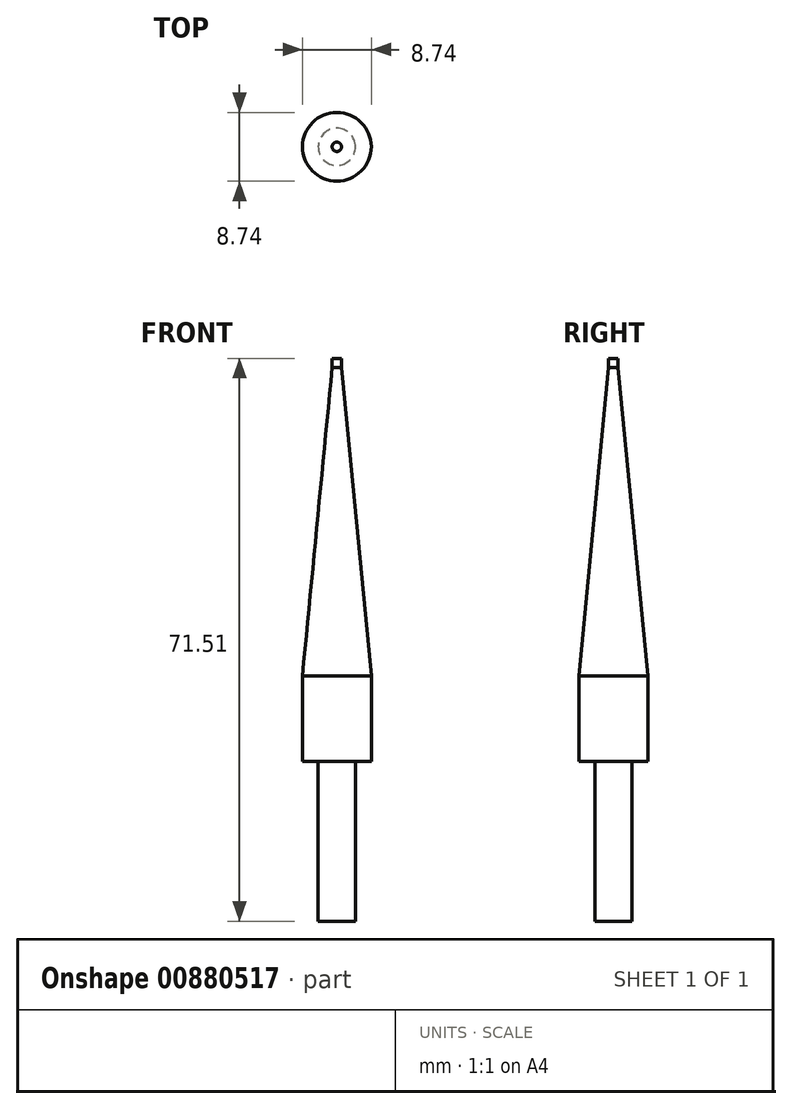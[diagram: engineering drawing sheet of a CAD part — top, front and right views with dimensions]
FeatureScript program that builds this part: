
annotation { "Feature Type Name" : "Feature", "Feature Type Description" : "" }
export const myFeature = defineFeature(function(context is Context, id is Id, definition is map)
    precondition{}
    {
        {
            var Q0;
            Q0=qCreatedBy(makeId("Front.planeOp"),FACE);
            var sketch = newSketch(context, id + "F0", { "sketchPlane" : qUnion([Q0])});
            skLineSegment(sketch, "E0", {"start": v(0.6, 55.68) * mm, "end": v(4.37, 16.5) * mm});
            skLineSegment(sketch, "E1", {"start": v(4.37, 16.5) * mm, "end": v(4.37, 5.65) * mm});
            skLineSegment(sketch, "E2", {"start": v(4.37, 5.65) * mm, "end": v(2.36, 5.65) * mm});
            skLineSegment(sketch, "E3", {"start": v(2.36, 5.65) * mm, "end": v(2.36, -14.67) * mm});
            skLineSegment(sketch, "E4", {"start": v(2.36, -14.67) * mm, "end": v(0, -14.67) * mm});
            skLineSegment(sketch, "E5", {"start": v(0, -14.67) * mm, "end": v(0, 56.84) * mm});
            skLineSegment(sketch, "E6", {"start": v(0, 56.84) * mm, "end": v(1, 56.84) * mm});
            skLineSegment(sketch, "E7", {"start": v(0, 56.84) * mm, "end": v(0, -14.67) * mm});
            skLineSegment(sketch, "E8", {"start": v(0.6, 55.67) * mm, "end": v(0.6, 55.68) * mm});
            skLineSegment(sketch, "E9", {"start": v(0.6, 55.68) * mm, "end": v(0.6, 60.51) * mm});
            skLineSegment(sketch, "E10", {"start": v(0.6, 60.51) * mm, "end": v(1, 56.84) * mm});
            skSolve(sketch);
        }
        {
            var Q0;
            Q0=makeQuery(id+"F0.imprint","IMPRINT",FACE,{"disambiguationData":[TD([[makeQuery(id+"F0.imprint","IMPRINT",EDGE,{"derivedFrom":sQuery(id+"F0.wireOp",EDGE,"E0")}),-1.0]])]});
            var Q1;
            Q1=sQuery(id+"F0.wireOp",EDGE,"E5");
            revolve(context, id + "F1", {"surfaceOperationType" : NewSurfaceOperationType.NEW, "entities" : qUnion([Q0]), "axis" : qUnion([Q1]), "revolveType" : RevolveType.FULL});
        }
    });
